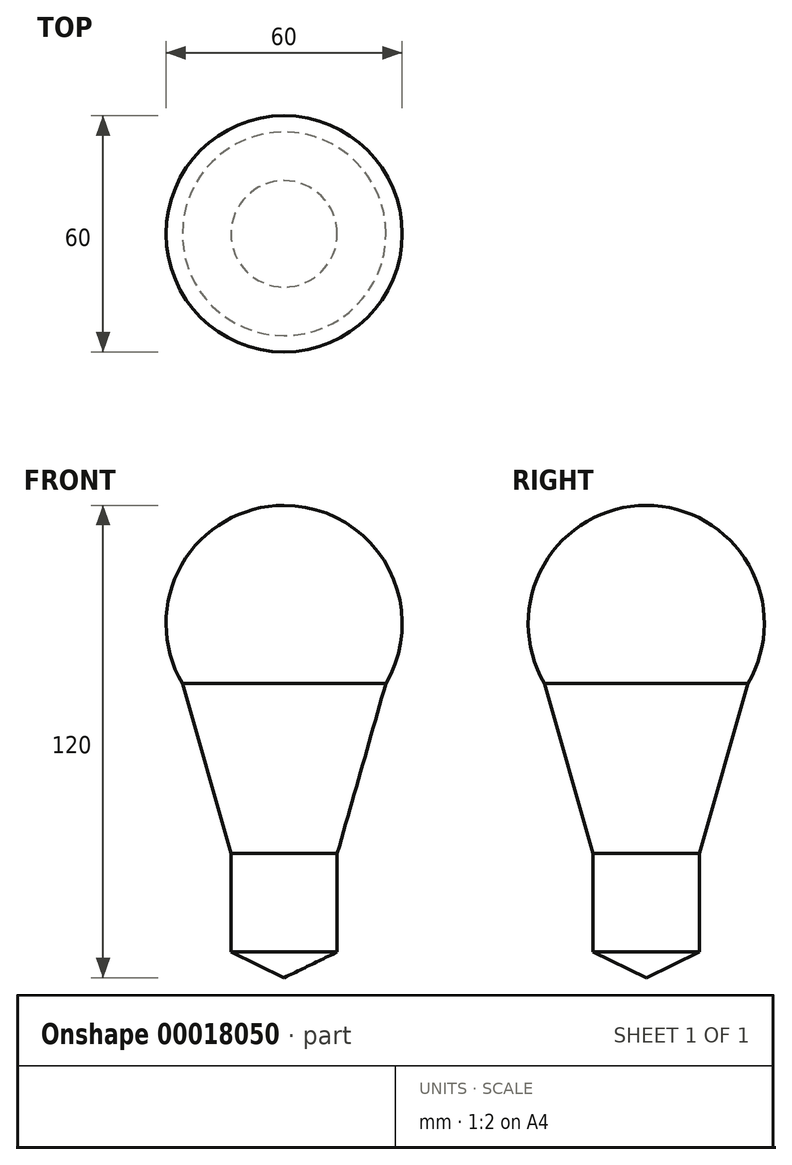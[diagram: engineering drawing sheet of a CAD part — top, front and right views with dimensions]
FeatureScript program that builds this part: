
annotation { "Feature Type Name" : "Feature", "Feature Type Description" : "" }
export const myFeature = defineFeature(function(context is Context, id is Id, definition is map)
    precondition{}
    {
        {
            var Q0;
            Q0=qCreatedBy(makeId("Front.planeOp"),FACE);
            var sketch = newSketch(context, id + "F0", { "sketchPlane" : qUnion([Q0])});
            skArc(sketch, "E0", {"start": v(51.73, 0) * mm, "mid": v(25.87, 45.2) * mm, "end": v(0, 0) * mm});
            skLineSegment(sketch, "E1", {"start": v(0, 0) * mm, "end": v(12.37, -43.27) * mm});
            skLineSegment(sketch, "E2", {"start": v(12.37, -43.27) * mm, "end": v(12.37, -68.27) * mm});
            skLineSegment(sketch, "E3", {"start": v(12.37, -68.27) * mm, "end": v(25.87, -74.8) * mm});
            skLineSegment(sketch, "E4", {"start": v(25.87, -74.8) * mm, "end": v(39.37, -68.27) * mm});
            skLineSegment(sketch, "E5", {"start": v(39.37, -68.27) * mm, "end": v(39.37, -43.27) * mm});
            skLineSegment(sketch, "E6", {"start": v(39.37, -43.27) * mm, "end": v(51.73, 0) * mm});
            skLineSegment(sketch, "E7", {"start": v(12.37, -43.27) * mm, "end": v(39.37, -43.27) * mm});
            skLineSegment(sketch, "E8", {"start": v(25.87, 45.2) * mm, "end": v(25.87, -74.8) * mm});
            skPoint(sketch, "E9.orphan", {"position": v(25.87, 88.8) * mm});
            skSolve(sketch);
        }
        {
            var Q0;
            {var subQ5=sQuery(id+"F0.wireOp",EDGE,"E1");Q0=makeQuery(id+"F0.imprint","IMPRINT",FACE,{"disambiguationData":[TD([[makeQuery(id+"F0.imprint","IMPRINT",EDGE,{"derivedFrom":subQ5}),1.0]])]});}
            var Q1;
            {var subQ4=sQuery(id+"F0.wireOp",EDGE,"E2");Q1=makeQuery(id+"F0.imprint","IMPRINT",FACE,{"disambiguationData":[TD([[makeQuery(id+"F0.imprint","IMPRINT",EDGE,{"derivedFrom":subQ4}),1.0]])]});}
            var Q2;
            Q2=sQuery(id+"F0.wireOp",EDGE,"E8");
            revolve(context, id + "F1", {"entities" : qUnion([Q0, Q1]), "axis" : qUnion([Q2]), "revolveType" : RevolveType.FULL});
        }
    });
